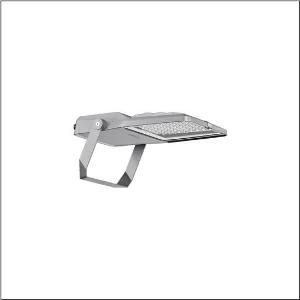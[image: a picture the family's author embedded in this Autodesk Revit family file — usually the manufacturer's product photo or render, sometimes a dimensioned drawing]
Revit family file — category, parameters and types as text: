
# Revit family: floodlight_fl_21_iq_mini___pl52_5xa7772d3d1a_25a1
name_source: partatom
category: Lighting Fixtures
units: mm (PartAtom-declared; Revit-internal decimal feet)

## family parameters
Cut with Voids When Loaded = No
Host = Face
Light Source = No
Part Type = Normal
Room Calculation Point = No
Round Connector Dimension = Use Diameter
Shared = No

## types (1)
- --- (1 x LED, 15340 lm, 143 W, 3000K)
    Apparent Load = 143 VA
    CIE Flux Codes = 26 60 98 100 100
    Color Rendering = 80
    Color Temperature = 3000K
    Default Elevation = 1800 mm
    Description = Floodlight FL 21 iQ mini, floodlight, primary light control with lens, of PMMA, primary optical cover: protective disc, of toughened safety glass, transparent, light distribution: PL52, light emission: direct distribution, installation type: surface-mounted, LED, High Power LED, rated luminous flux: 15.340lm, luminous efficacy: 107lm/W, light colour: 830, colour temperature: 3000K, control: Street-Remote, Auto-Match, Temp-Guard, Night-Set, Smart-Wire, Desk-Remote (wireless, voltage-free reading and setting of iQ features in the workshop via application-optimized NFC function/RFID function), optimised constant luminous flux control (CLO 2.0), with terminal, 6-pole, mains connection: 220..240V, AC, 50/60Hz, start of lifetime: 143W, end of service life: 152W, reduction: 61W, luminaire housing, of diecast aluminium, powder-coated, Siteco® metallic grey (DB 702S), corrosivity category C5 mid according to DIN EN ISO 12944, sealing non-destructively replaceable, mounting bracket, of steel, galvanised, powder-coated, Siteco® metallic grey (DB 702S), protection rating (complete): IP66, insulation class (complete): insulation class II (safety insulation), certification: CE, ENEC, VDE, protection symbol: D, impact resistance: IK08, permissible operating ambient temperature: -40..+40°C, permissible operating ambient temperature for outdoor applications: -40..+50°C, standard: DIN EN 12944, LABS conformity tested according to VDMA 24364:2018-05, packaging unit: 1 piece

Light Distribution: PL52
    Height = 70 mm
    Lamp = 1 x LED
    Lamp Light Flux = 15340 lm
    Lamp Power = 143 W
    Lamp count = 1
    Length = 485 mm
    Luminous efficacy = 107 lm/W
    Manufacturer = Siteco
    ModVariant = No
    Model = 5XA7772D3D1A
    Number of Poles = 1
    OnlyDefault = Yes
    Power Factor = 1
    Product Name = Floodlight FL 21 iQ mini | PL52
    Product group = floodlight | pylon annexe
    ProductGroupID = 6200
    Protection Class = Protection class II
    Protection Degree = IP 66
    RLX_Detail_Level = 1
    RLX_Emergency_Light_Flux = 0 lm
    RLX_Emergency_Type = 0
    RLX_Emergency_Type_DB = No
    RlxData = <blob elided: 96709 chars, md5=45dd3dca>
    Socket = socket
    Standby Power = 0 W
    System Light Flux = 15340 lm
    System Power = 143 W
    Type Comments = factory setting: luminous flux: 100 % | dim-lin: 254 | 730 mA
    Type Image = l_1006845.jpg
    URL = http://relux.com
    VarID = @adj_095973
    Voltage = 0 V
    Weight = 0.00 kg
    Width = 337 mm

## geometry (parser evidence)
native form markers: Blend x4, Sweep x14
no freeform markers — native parametric forms only
